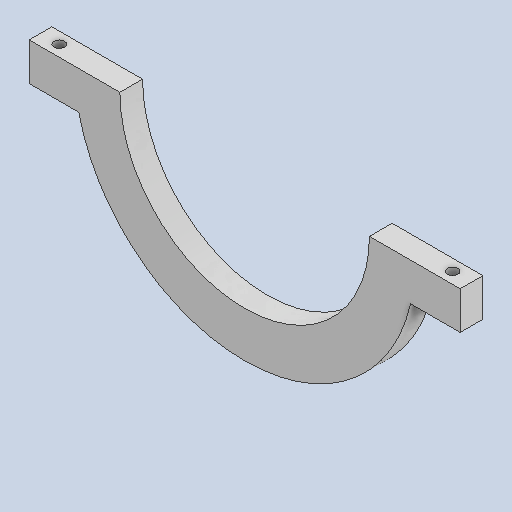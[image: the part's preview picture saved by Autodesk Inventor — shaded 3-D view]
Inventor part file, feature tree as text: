
AUTODESK INVENTOR PART (.ipt)
format: ipt  version: 2025 (Build 290162010, 162A)  size: 154,112 bytes
history: native  units: mm
features: extrude x2, sketch x2, mirror x1, other x1
ambient origin geometry x8: Origin, YZ Plane, XZ Plane, XY Plane, X Axis, Y Axis, Z Axis, Center Point
bodies: Solid1 (feature_tree)
feature tree (6):
  extrude  "Extrusion1"  Depth=30.0mm
  extrude  "Extrusion7"  Depth=50.0mm
  mirror  "Mirror1"
  sketch  "Sketch1"  dims[d2=30.0mm d3=0.0mm d13=390.0mm]
  sketch  "Sketch7"  dims[d26=80.0mm d36=60.0mm d40=60.0mm d41=50.0mm d42=14.0mm d43=25.0mm d44=0.0mm d45=0.0mm]
  other  "Definition1"
